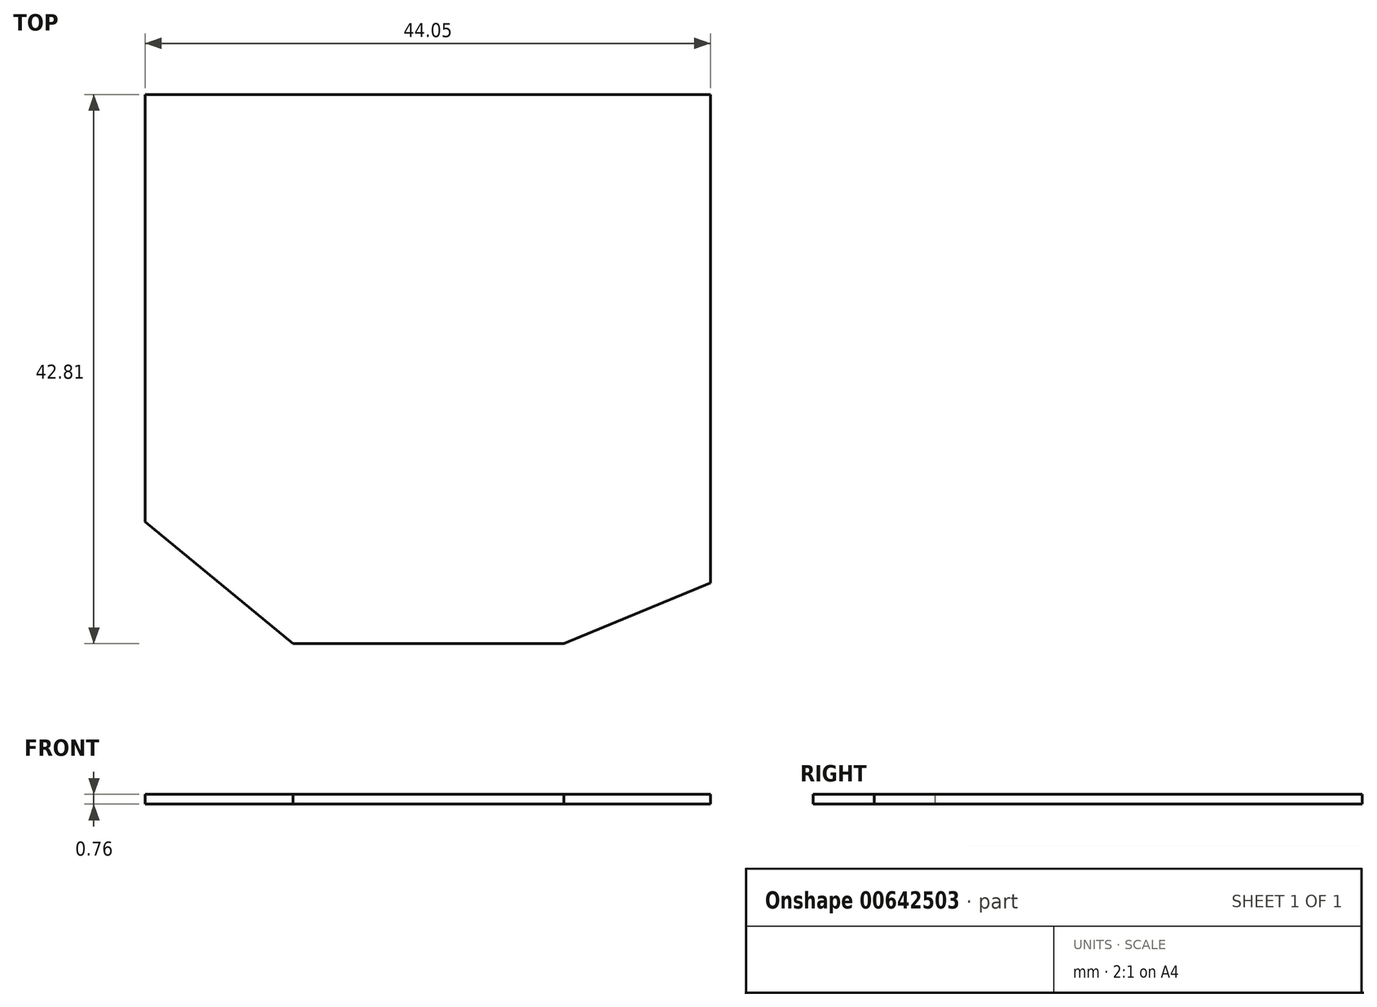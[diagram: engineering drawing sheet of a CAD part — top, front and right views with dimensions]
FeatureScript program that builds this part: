
annotation { "Feature Type Name" : "Feature", "Feature Type Description" : "" }
export const myFeature = defineFeature(function(context is Context, id is Id, definition is map)
    precondition{}
    {
        {
            var Q0;
            Q0=qCreatedBy(makeId("Top.planeOp"),FACE);
            var sketch = newSketch(context, id + "F0", { "sketchPlane" : qUnion([Q0])});
            skLineSegment(sketch, "E0.bottom", {"start": v(0, 0) * mm, "end": v(44.05, 0) * mm});
            skLineSegment(sketch, "E0.top", {"start": v(11.51, -42.81) * mm, "end": v(32.63, -42.81) * mm});
            skLineSegment(sketch, "E0.left", {"start": v(0, 0) * mm, "end": v(0, -33.3) * mm});
            skLineSegment(sketch, "E0.right", {"start": v(44.05, 0) * mm, "end": v(44.05, -38.05) * mm});
            skLineSegment(sketch, "E1", {"start": v(0, -33.3) * mm, "end": v(11.51, -42.81) * mm});
            skLineSegment(sketch, "E2", {"start": v(32.63, -42.81) * mm, "end": v(44.05, -38.05) * mm});
            skSolve(sketch);
        }
        {
            var Q0;
            Q0=makeQuery(id+"F0.imprint","IMPRINT",FACE,{"disambiguationData":[TD([[makeQuery(id+"F0.imprint","IMPRINT",EDGE,{"derivedFrom":sQuery(id+"F0.wireOp",EDGE,"E0.bottom")}),-1.0]])]});
            extrude(context, id + "F1", {"entities" : qUnion([Q0]), "depth" : 0.76 * mm, "offsetDistance" : 25.4 * mm});
        }
    });
